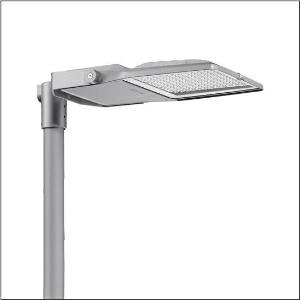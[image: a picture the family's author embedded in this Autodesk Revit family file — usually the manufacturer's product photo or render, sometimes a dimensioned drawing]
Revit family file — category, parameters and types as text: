
# Revit family: floodlight_fl_21_iq_midi___pl43_5xa7782e2a3a_72be
name_source: partatom
category: Lighting Fixtures
units: mm (PartAtom-declared; Revit-internal decimal feet)

## family parameters
Cut with Voids When Loaded = No
Host = Face
Light Source = No
Part Type = Normal
Room Calculation Point = No
Round Connector Dimension = Use Diameter
Shared = No

## types (1)
- --- (1 x LED, 27540 lm, 208.1 W, 3000K)
    Apparent Load = 208 VA
    CIE Flux Codes = 27 78 99 100 100
    Color Rendering = 70
    Color Temperature = 3000K
    Default Elevation = 1800 mm
    Description = Floodlight FL 21 iQ midi, floodlight, primary light control with lens, of PMMA, primary optical cover: protective disc, of toughened safety glass, transparent, light distribution: PL43, light emission: direct distribution, installation type: surface-mounted, LED, High Power LED, rated luminous flux: 27.540lm, luminous efficacy: 132lm/W, light colour: 730, colour temperature: 3000K, control gear: ECG iQ, control: optimised constant luminous flux control (CLO 2.0), Desk-Remote (wireless, voltage-free reading and setting of iQ features in the workshop via application-optimized NFC function/RFID function), Smart-Wire, Night-Set, Temp-Guard, Auto-Match, Street-Remote, with terminal, 6-pole, mains connection: 220..240V, AC, 50/60Hz, start of lifetime: 208W, end of service life: 227W, reduction: 90W, luminaire housing, of diecast aluminium, powder-coated, Siteco® metallic grey (DB 702S), corrosivity category C5 mid according to DIN EN ISO 12944, sealing non-destructively replaceable, please order mast flange separately, mast bracket, of steel, galvanised, powder-coated, Siteco® metallic grey (DB 702S), protection rating (complete): IP66, insulation class (complete): insulation class II (safety insulation), certification: CE, ENEC, VDE, protection symbol: D, impact resistance: IK08, permissible operating ambient temperature: -40..+40°C, permissible operating ambient temperature for outdoor applications: -40..+50°C, standard: DIN EN 12944, LABS conformity tested according to VDMA 24364:2018-05, packaging unit: 1 piece

Light Distribution: PL43
    Height = 76 mm
    Lamp = 1 x LED
    Lamp Light Flux = 27540 lm
    Lamp Power = 208.1 W
    Lamp count = 1
    Length = 657 mm
    Luminous efficacy = 132 lm/W
    Manufacturer = Siteco
    ModVariant = No
    Model = 5XA7782E2A3A
    Number of Poles = 1
    OnlyDefault = Yes
    Power Factor = 1
    Product Name = Floodlight FL 21 iQ midi | PL43
    Product group = floodlight | pylon annexe
    ProductGroupID = 6200
    Protection Class = Protection class II
    Protection Degree = IP 66
    RLX_Detail_Level = 1
    RLX_Emergency_Light_Flux = 0 lm
    RLX_Emergency_Type = 0
    RLX_Emergency_Type_DB = No
    RlxData = <blob elided: 153601 chars, md5=dfa4326d>
    Socket = socket
    Standby Power = 0 W
    System Light Flux = 27540 lm
    System Power = 208 W
    Type Comments = factory setting: luminous flux: 100 % | dim-lin: 254 | 710 mA
    Type Image = l_1007123.jpg
    URL = http://relux.com
    VarID = @adj_074033
    Voltage = 0 V
    Weight = 0.00 kg
    Width = 442 mm

## geometry (parser evidence)
native form markers: Blend x4, Sweep x12
no freeform markers — native parametric forms only
